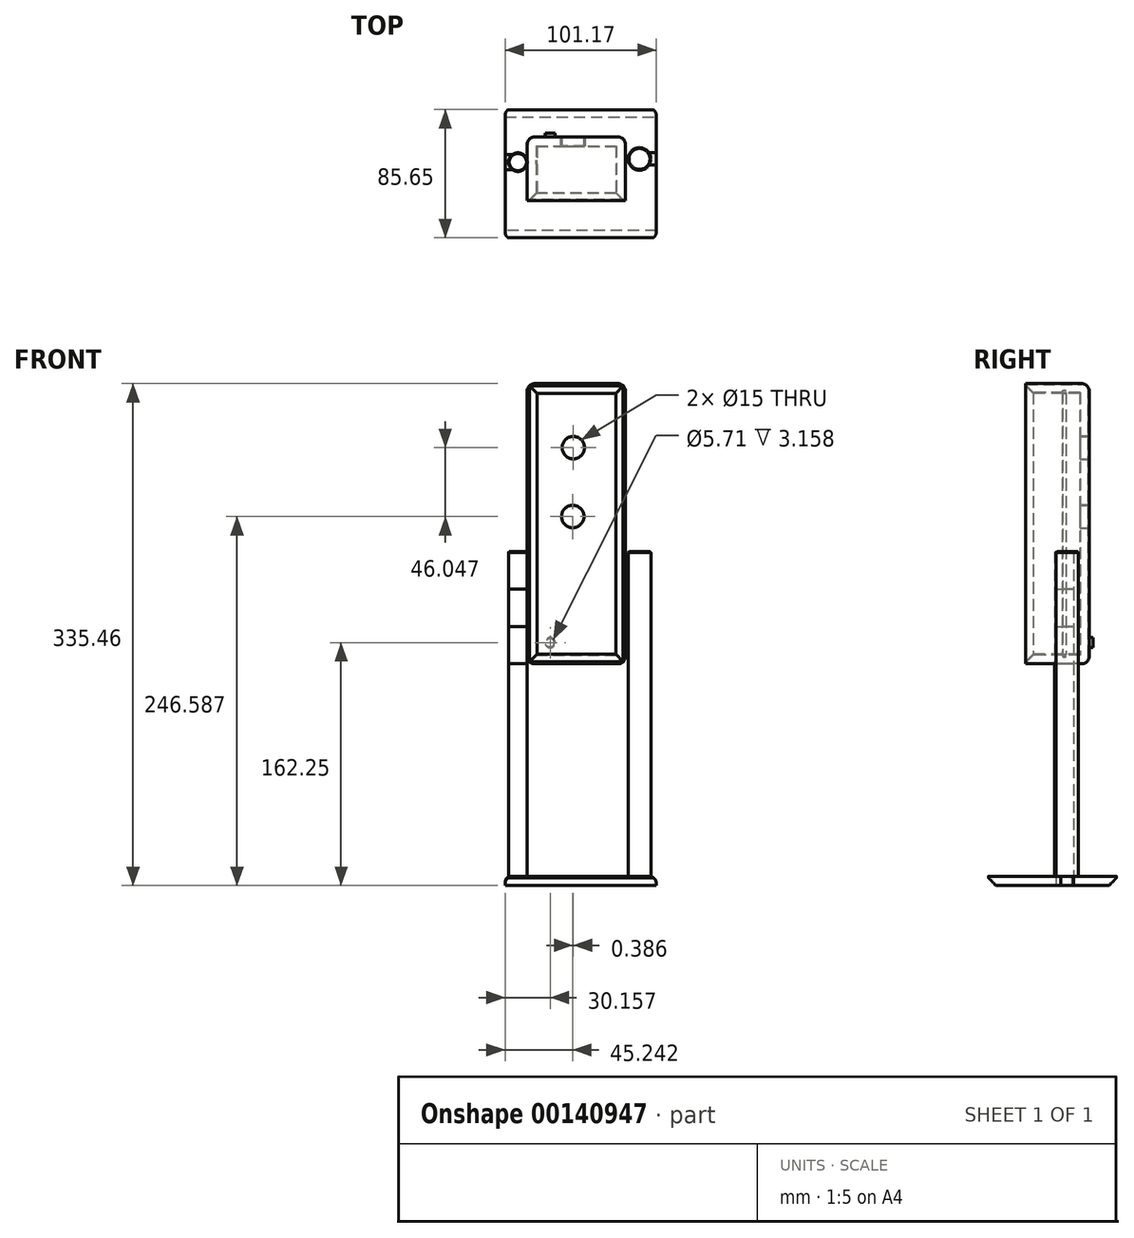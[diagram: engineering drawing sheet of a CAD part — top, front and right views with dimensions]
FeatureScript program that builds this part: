
annotation { "Feature Type Name" : "Feature", "Feature Type Description" : "" }
export const myFeature = defineFeature(function(context is Context, id is Id, definition is map)
    precondition{}
    {
        {
            var Q0;
            Q0=qCreatedBy(makeId("Top.planeOp"),FACE);
            var sketch = newSketch(context, id + "F0", { "sketchPlane" : qUnion([Q0])});
            skLineSegment(sketch, "E0.bottom", {"start": v(-55.8, -35.83) * mm, "end": v(45.37, -35.83) * mm});
            skLineSegment(sketch, "E0.top", {"start": v(-55.8, 49.82) * mm, "end": v(45.37, 49.82) * mm});
            skLineSegment(sketch, "E0.left", {"start": v(-55.8, -35.83) * mm, "end": v(-55.8, 49.82) * mm});
            skLineSegment(sketch, "E0.right", {"start": v(45.37, -35.83) * mm, "end": v(45.37, 49.82) * mm});
            skSolve(sketch);
        }
        {
            var Q0;
            Q0=makeQuery(id+"F0.imprint","IMPRINT",FACE,{"disambiguationData":[TD([[makeQuery(id+"F0.imprint","IMPRINT",EDGE,{"derivedFrom":sQuery(id+"F0.wireOp",EDGE,"E0.bottom")}),1.0]])]});
            extrude(context, id + "F1", {"entities" : qUnion([Q0]), "depth" : 6 * mm});
        }
        {
            var Q0;
            Q0=makeQuery(id+"F1.opExtrude","CAP_FACE",FACE,{"disambiguationData":[OSD([sQuery(id+"F0.wireOp",EDGE,"E0.bottom"),sQuery(id+"F0.wireOp",EDGE,"E0.top"),sQuery(id+"F0.wireOp",EDGE,"E0.left"),sQuery(id+"F0.wireOp",EDGE,"E0.right")])],"isStart":false});
            var sketch = newSketch(context, id + "F19", { "sketchPlane" : qUnion([Q0])});
            skCircle(sketch, "E1", {"center": v(-47.26, 14.75) * mm, "radius": 6.27 * mm});
            skSolve(sketch);
        }
        {
            var Q0;
            Q0=makeQuery(id+"F19.imprint","IMPRINT",FACE,{"disambiguationData":[TD([[makeQuery(id+"F19.imprint","IMPRINT",EDGE,{"derivedFrom":sQuery(id+"F19.wireOp",EDGE,"E1")}),1.0]])]});
            extrude(context, id + "F20", {"entities" : qUnion([Q0]), "operationType" : NewBodyOperationType.ADD, "depth" : 142.1 * mm});
        }
        {
            var Q0;
            Q0=makeQuery(id+"F1.opExtrude","CAP_FACE",FACE,{"disambiguationData":[OSD([sQuery(id+"F0.wireOp",EDGE,"E0.bottom"),sQuery(id+"F0.wireOp",EDGE,"E0.top"),sQuery(id+"F0.wireOp",EDGE,"E0.left"),sQuery(id+"F0.wireOp",EDGE,"E0.right")])],"isStart":false});
            var sketch = newSketch(context, id + "F2", { "sketchPlane" : qUnion([Q0])});
            skCircle(sketch, "E2", {"center": v(34.1, 16.88) * mm, "radius": 7.55 * mm});
            skSolve(sketch);
        }
        {
            var Q0;
            Q0=makeQuery(id+"F2.imprint","IMPRINT",FACE,{"disambiguationData":[TD([[makeQuery(id+"F2.imprint","IMPRINT",EDGE,{"derivedFrom":sQuery(id+"F2.wireOp",EDGE,"E2")}),1.0]])]});
            extrude(context, id + "F3", {"entities" : qUnion([Q0]), "operationType" : NewBodyOperationType.ADD, "depth" : 132.12 * mm});
        }
        {
            var Q0;
            Q0=makeQuery(id+"F3.opExtrude","CAP_FACE",FACE,{"disambiguationData":[OSD([sQuery(id+"F2.wireOp",EDGE,"E2")])],"isStart":false});
            extrude(context, id + "F4", {"entities" : qUnion([Q0]), "operationType" : NewBodyOperationType.ADD, "depth" : 10.04 * mm});
        }
        {
            var Q0;
            Q0=makeQuery(id+"F20.opExtrude","CAP_FACE",FACE,{"disambiguationData":[OSD([sQuery(id+"F19.wireOp",EDGE,"E1")])],"isStart":false});
            var sketch = newSketch(context, id + "F21", { "sketchPlane" : qUnion([Q0])});
            skLineSegment(sketch, "E3.bottom", {"start": v(-41.04, 31.6) * mm, "end": v(24.72, 31.6) * mm});
            skLineSegment(sketch, "E3.top", {"start": v(-41.04, -11) * mm, "end": v(24.72, -11) * mm});
            skLineSegment(sketch, "E3.left", {"start": v(-41.04, 31.6) * mm, "end": v(-41.04, -11) * mm});
            skLineSegment(sketch, "E3.right", {"start": v(24.72, 31.6) * mm, "end": v(24.72, -11) * mm});
            skSolve(sketch);
        }
        {
            var Q0;
            {var subQ4=sQuery(id+"F21.wireOp",EDGE,"E3.bottom");Q0=makeQuery(id+"F21.imprint","IMPRINT",FACE,{"disambiguationData":[TD([[makeQuery(id+"F21.imprint","IMPRINT",EDGE,{"derivedFrom":subQ4}),-1.0]])]});}
            extrude(context, id + "F5", {"entities" : qUnion([Q0]), "depth" : 187.36 * mm});
        }
        {
            var Q0;
            Q0=makeQuery(id+"F4.opExtrude","CAP_FACE",FACE,{"disambiguationData":[OSD([sQuery(id+"F2.wireOp",EDGE,"E2")])],"isStart":false});
            extrude(context, id + "F22", {"entities" : qUnion([Q0]), "operationType" : NewBodyOperationType.ADD, "depth" : 25 * mm});
        }
        {
            var Q0;
            Q0=makeQuery(id+"F20.opExtrude","CAP_FACE",FACE,{"disambiguationData":[OSD([sQuery(id+"F19.wireOp",EDGE,"E1")])],"isStart":false});
            extrude(context, id + "F23", {"entities" : qUnion([Q0]), "depth" : 25 * mm});
        }
        {
            var Q0;
            Q0=makeQuery(id+"F23.opExtrude","CAP_FACE",FACE,{"disambiguationData":[OSD([sQuery(id+"F19.wireOp",EDGE,"E1")])],"isStart":false});
            extrude(context, id + "F6", {"entities" : qUnion([Q0]), "depth" : 25 * mm});
        }
        {
            var Q0;
            Q0=makeQuery(id+"F22.opExtrude","CAP_FACE",FACE,{"disambiguationData":[OSD([sQuery(id+"F2.wireOp",EDGE,"E2")])],"isStart":false});
            extrude(context, id + "F24", {"entities" : qUnion([Q0]), "operationType" : NewBodyOperationType.ADD, "depth" : 25 * mm});
        }
        {
            var Q0;
            Q0=makeQuery(id+"F24.opExtrude","CAP_FACE",FACE,{"disambiguationData":[OSD([sQuery(id+"F2.wireOp",EDGE,"E2")])],"isStart":false});
            extrude(context, id + "F7", {"entities" : qUnion([Q0]), "operationType" : NewBodyOperationType.ADD, "depth" : 25 * mm});
        }
        {
            var Q0;
            Q0=makeQuery(id+"F6.opExtrude","CAP_FACE",FACE,{"disambiguationData":[OSD([sQuery(id+"F19.wireOp",EDGE,"E1")])],"isStart":false});
            var sketch = newSketch(context, id + "F25", { "sketchPlane" : qUnion([Q0])});
            skSolve(sketch);
        }
        {
            var Q0;
            Q0 = qSketchRegion(id + "F25", true);
            var Q1;
            Q1=makeQuery(id+"F25.imprint","IMPRINT",FACE,{"disambiguationData":[TD([[makeQuery(id+"F25.imprint","IMPRINT",EDGE,{"derivedFrom":makeQuery(id+"F6.opExtrude","CAP_EDGE",EDGE,{"disambiguationData":[OSD([sQuery(id+"F19.wireOp",EDGE,"E1")])],"isStart":false})}),1.0]])]});
            extrude(context, id + "F8", {"entities" : qUnion([Q0, Q1]), "depth" : 25 * mm});
        }
        {
            var Q0;
            Q0=makeQuery(id+"F1.opExtrude","CAP_EDGE",EDGE,{"disambiguationData":[OSD([sQuery(id+"F0.wireOp",EDGE,"E0.left")])],"isStart":false});
            fillet(context, id + "F26", {"entities" : qUnion([Q0]), "radius" : 5 * mm, "tangentPropagation" : true, "allowEdgeOverflow" : false});
        }
        {
            var Q0;
            Q0=makeQuery(id+"F1.opExtrude","CAP_EDGE",EDGE,{"disambiguationData":[OSD([sQuery(id+"F0.wireOp",EDGE,"E0.right")])],"isStart":false});
            fillet(context, id + "F9", {"entities" : qUnion([Q0]), "radius" : 5 * mm, "tangentPropagation" : true, "allowEdgeOverflow" : false});
        }
        {
            var Q0;
            Q0=makeQuery(id+"F1.opExtrude","CAP_EDGE",EDGE,{"disambiguationData":[OSD([sQuery(id+"F0.wireOp",EDGE,"E0.bottom")])],"isStart":true});
            chamfer(context, id + "F10", {"entities" : qUnion([Q0]), "width" : 5 * mm, "tangentPropagation" : true});
        }
        {
            var Q0;
            Q0=makeQuery(id+"F1.opExtrude","CAP_EDGE",EDGE,{"disambiguationData":[OSD([sQuery(id+"F0.wireOp",EDGE,"E0.top")])],"isStart":true});
            chamfer(context, id + "F27", {"entities" : qUnion([Q0]), "width" : 5 * mm, "tangentPropagation" : true});
        }
        {
            var Q0;
            Q0=makeQuery(id+"F5.opExtrude","SWEPT_FACE",FACE,{"disambiguationData":[OSD([sQuery(id+"F21.wireOp",EDGE,"E3.top")])]});
            shell(context, id + "F28", {"entities" : qUnion([Q0]), "thickness" : 6.5 * mm});
        }
        {
            var Q0;
            {var subQ0=sQuery(id+"F21.wireOp",EDGE,"E3.left");Q0=makeQuery(id+"F5.opExtrude","CAP_EDGE",EDGE,{"disambiguationData":[OSD([subQ0]),TDD([makeQuery(id+"F21.imprint","IMPRINT",EDGE,{"disambiguationData":[TD([[makeQuery(id+"F21.imprint","INTERSECT",VERTEX,{"derivedFrom":[sQuery(id+"F21.wireOp",EDGE,"E3.bottom"),subQ0]}),-1.0]])],"derivedFrom":subQ0})])],"isStart":true});}
            var Q1;
            Q1=makeQuery(id+"F5.opExtrude","SWEPT_FACE",FACE,{"disambiguationData":[OSD([sQuery(id+"F21.wireOp",EDGE,"E3.bottom")])]});
            var Q2;
            {var subQ0=sQuery(id+"F21.wireOp",EDGE,"E3.left");Q2=makeQuery(id+"F5.opExtrude","SWEPT_FACE",FACE,{"disambiguationData":[OSD([subQ0]),TDD([makeQuery(id+"F21.imprint","IMPRINT",EDGE,{"disambiguationData":[TD([[makeQuery(id+"F21.imprint","INTERSECT",VERTEX,{"derivedFrom":[sQuery(id+"F21.wireOp",EDGE,"E3.bottom"),subQ0]}),-1.0]])],"derivedFrom":subQ0})])]});}
            fillet(context, id + "F29", {"entities" : qUnion([Q0, Q1, Q2]), "radius" : 5 * mm, "tangentPropagation" : true, "allowEdgeOverflow" : false});
        }
        {
            var Q0;
            Q0=makeQuery(id+"F5.opExtrude","SWEPT_FACE",FACE,{"disambiguationData":[OSD([sQuery(id+"F21.wireOp",EDGE,"E3.bottom")])]});
            var sketch = newSketch(context, id + "F11", { "sketchPlane" : qUnion([Q0])});
            skCircle(sketch, "E4", {"center": v(10.17, 292.63) * mm, "radius": 7.28 * mm});
            skSolve(sketch);
        }
        {
            var Q0;
            Q0=makeQuery(id+"F11.imprint","IMPRINT",FACE,{"disambiguationData":[TD([[makeQuery(id+"F11.imprint","IMPRINT",EDGE,{"derivedFrom":sQuery(id+"F11.wireOp",EDGE,"E4")}),-1.0]])]});
            var sketch = newSketch(context, id + "F12", { "sketchPlane" : qUnion([Q0])});
            skCircle(sketch, "E5", {"center": v(10.56, 246.59) * mm, "radius": 7.37 * mm});
            skSolve(sketch);
        }
        {
            var Q0;
            Q0=sQuery(id+"F11.wireOp",VERTEX,"E4.center");
            var Q1;
            Q1=makeQuery(id+"F5.opExtrude","SWEPT_BODY",BODY,{"disambiguationData":[OSD([sQuery(id+"F19.wireOp",EDGE,"E1"),sQuery(id+"F21.wireOp",EDGE,"E3.bottom"),sQuery(id+"F21.wireOp",EDGE,"E3.top"),sQuery(id+"F21.wireOp",EDGE,"E3.left"),sQuery(id+"F21.wireOp",EDGE,"E3.right")])]});
            hole(context, id + "F13", {"style" : HoleStyle.SIMPLE, "endStyle" : HoleEndStyle.THROUGH, "holeDiameter" : 15 * mm, "locations" : qUnion([Q0]), "scope" : qUnion([Q1]), "isTappedThrough" : true});
        }
        {
            var Q0;
            Q0=sQuery(id+"F12.wireOp",VERTEX,"E5.center");
            var Q1;
            Q1=makeQuery(id+"F5.opExtrude","SWEPT_BODY",BODY,{"disambiguationData":[OSD([sQuery(id+"F19.wireOp",EDGE,"E1"),sQuery(id+"F21.wireOp",EDGE,"E3.bottom"),sQuery(id+"F21.wireOp",EDGE,"E3.top"),sQuery(id+"F21.wireOp",EDGE,"E3.left"),sQuery(id+"F21.wireOp",EDGE,"E3.right")])]});
            hole(context, id + "F14", {"style" : HoleStyle.SIMPLE, "endStyle" : HoleEndStyle.THROUGH, "holeDiameter" : 15 * mm, "locations" : qUnion([Q0]), "scope" : qUnion([Q1]), "isTappedThrough" : true});
        }
        {
            var Q0;
            {var subQ0=sQuery(id+"F21.wireOp",EDGE,"E3.top");Q0=makeQuery(id+"F28.opShell","OFFSET_EDGE",EDGE,{"disambiguationData":[OSD([subQ0]),TDD([makeQuery(id+"F5.opExtrude","CAP_EDGE",EDGE,{"disambiguationData":[OSD([subQ0])],"isStart":true})])]});}
            var Q1;
            Q1=makeQuery(id+"F28.opShell","OFFSET_EDGE",EDGE,{"disambiguationData":[OSD([sQuery(id+"F21.wireOp",EDGE,"E3.top"),sQuery(id+"F21.wireOp",EDGE,"E3.left")])]});
            var Q2;
            Q2=makeQuery(id+"F28.opShell","OFFSET_EDGE",EDGE,{"disambiguationData":[OSD([sQuery(id+"F21.wireOp",EDGE,"E3.top"),sQuery(id+"F21.wireOp",EDGE,"E3.right")])]});
            var Q3;
            {var subQ0=sQuery(id+"F21.wireOp",EDGE,"E3.top");Q3=makeQuery(id+"F28.opShell","OFFSET_EDGE",EDGE,{"disambiguationData":[OSD([subQ0]),TDD([makeQuery(id+"F5.opExtrude","CAP_EDGE",EDGE,{"disambiguationData":[OSD([subQ0])],"isStart":false})])]});}
            chamfer(context, id + "F15", {"entities" : qUnion([Q0, Q1, Q2, Q3]), "width" : 5 * mm, "tangentPropagation" : true});
        }
        {
            var Q0;
            Q0=makeQuery(id+"F5.opExtrude","SWEPT_FACE",FACE,{"disambiguationData":[OSD([sQuery(id+"F21.wireOp",EDGE,"E3.bottom")])]});
            var sketch = newSketch(context, id + "F30", { "sketchPlane" : qUnion([Q0])});
            skCircle(sketch, "E6", {"center": v(25.64, 162.25) * mm, "radius": 3.35 * mm});
            skSolve(sketch);
        }
        {
            var Q0;
            Q0=makeQuery(id+"F30.imprint","IMPRINT",FACE,{"disambiguationData":[TD([[makeQuery(id+"F30.imprint","IMPRINT",EDGE,{"derivedFrom":sQuery(id+"F30.wireOp",EDGE,"E6")}),1.0]])]});
            extrude(context, id + "F31", {"entities" : qUnion([Q0]), "operationType" : NewBodyOperationType.ADD, "depth" : 2.66 * mm});
        }
        {
            var Q0;
            Q0=makeQuery(id+"F7.opExtrude","CAP_EDGE",EDGE,{"disambiguationData":[OSD([sQuery(id+"F2.wireOp",EDGE,"E2")])],"isStart":false});
            chamfer(context, id + "F16", {"entities" : qUnion([Q0]), "width" : 0.5 * mm, "tangentPropagation" : true});
        }
        {
            var Q0;
            Q0=makeQuery(id+"F8.opExtrude","CAP_EDGE",EDGE,{"disambiguationData":[OSD([sQuery(id+"F19.wireOp",EDGE,"E1")])],"isStart":false});
            chamfer(context, id + "F32", {"entities" : qUnion([Q0]), "width" : 0.5 * mm, "tangentPropagation" : true});
        }
        {
            var Q0;
            Q0=makeQuery(id+"F5.opExtrude","CAP_EDGE",EDGE,{"disambiguationData":[OSD([sQuery(id+"F21.wireOp",EDGE,"E3.right")])],"isStart":false});
            fillet(context, id + "F17", {"entities" : qUnion([Q0]), "radius" : 5 * mm, "tangentPropagation" : true, "allowEdgeOverflow" : false});
        }
        {
            var Q0;
            Q0=makeQuery(id+"F5.opExtrude","CAP_EDGE",EDGE,{"disambiguationData":[OSD([sQuery(id+"F21.wireOp",EDGE,"E3.right")])],"isStart":true});
            fillet(context, id + "F33", {"entities" : qUnion([Q0]), "radius" : 5 * mm, "tangentPropagation" : true, "allowEdgeOverflow" : false});
        }
        {
            var Q0;
            Q0=makeQuery(id+"F31.opExtrude","CAP_FACE",FACE,{"disambiguationData":[OSD([sQuery(id+"F30.wireOp",EDGE,"E6")])],"isStart":false});
            shell(context, id + "F18", {"entities" : qUnion([Q0]), "thickness" : 0.5 * mm});
        }
    });
